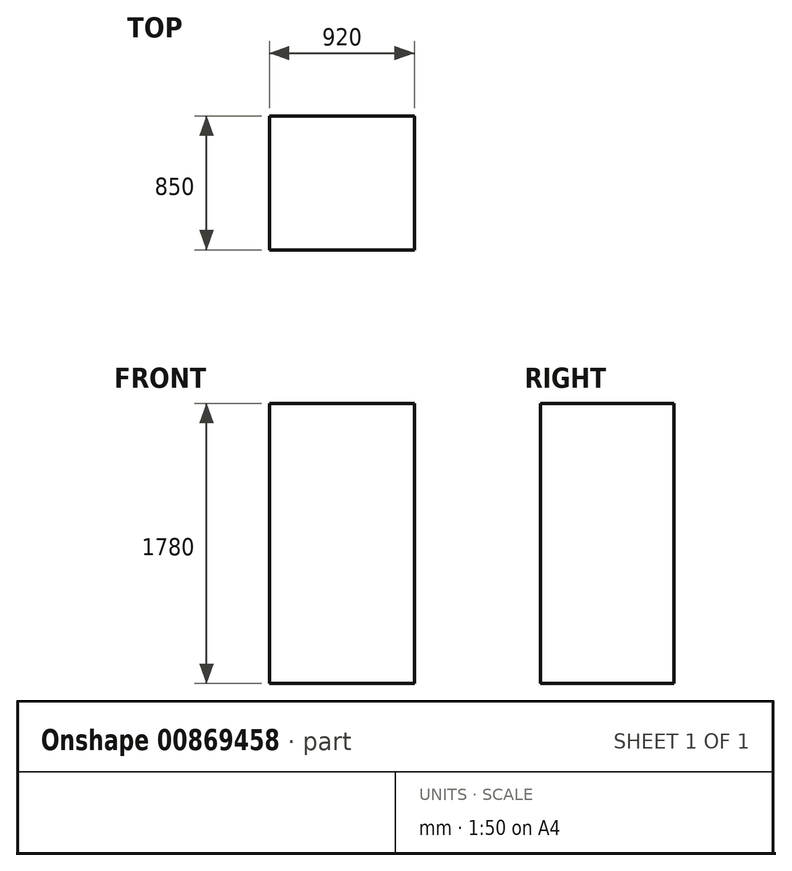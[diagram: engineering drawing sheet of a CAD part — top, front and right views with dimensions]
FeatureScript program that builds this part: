
annotation { "Feature Type Name" : "Feature", "Feature Type Description" : "" }
export const myFeature = defineFeature(function(context is Context, id is Id, definition is map)
    precondition{}
    {
        {
            var Q0;
            Q0=qCreatedBy(makeId("Top.planeOp"),FACE);
            var sketch = newSketch(context, id + "F0", { "sketchPlane" : qUnion([Q0])});
            skLineSegment(sketch, "E0.bottom", {"start": v(0, 0) * mm, "end": v(920, 0) * mm});
            skLineSegment(sketch, "E0.top", {"start": v(0, 850) * mm, "end": v(920, 850) * mm});
            skLineSegment(sketch, "E0.left", {"start": v(0, 0) * mm, "end": v(0, 850) * mm});
            skLineSegment(sketch, "E0.right", {"start": v(920, 0) * mm, "end": v(920, 850) * mm});
            skSolve(sketch);
        }
        {
            var Q0;
            Q0 = qSketchRegion(id + "F0", true);
            extrude(context, id + "F1", {"entities" : qUnion([Q0]), "depth" : 1780 * mm, "offsetDistance" : 25 * mm});
        }
    });
